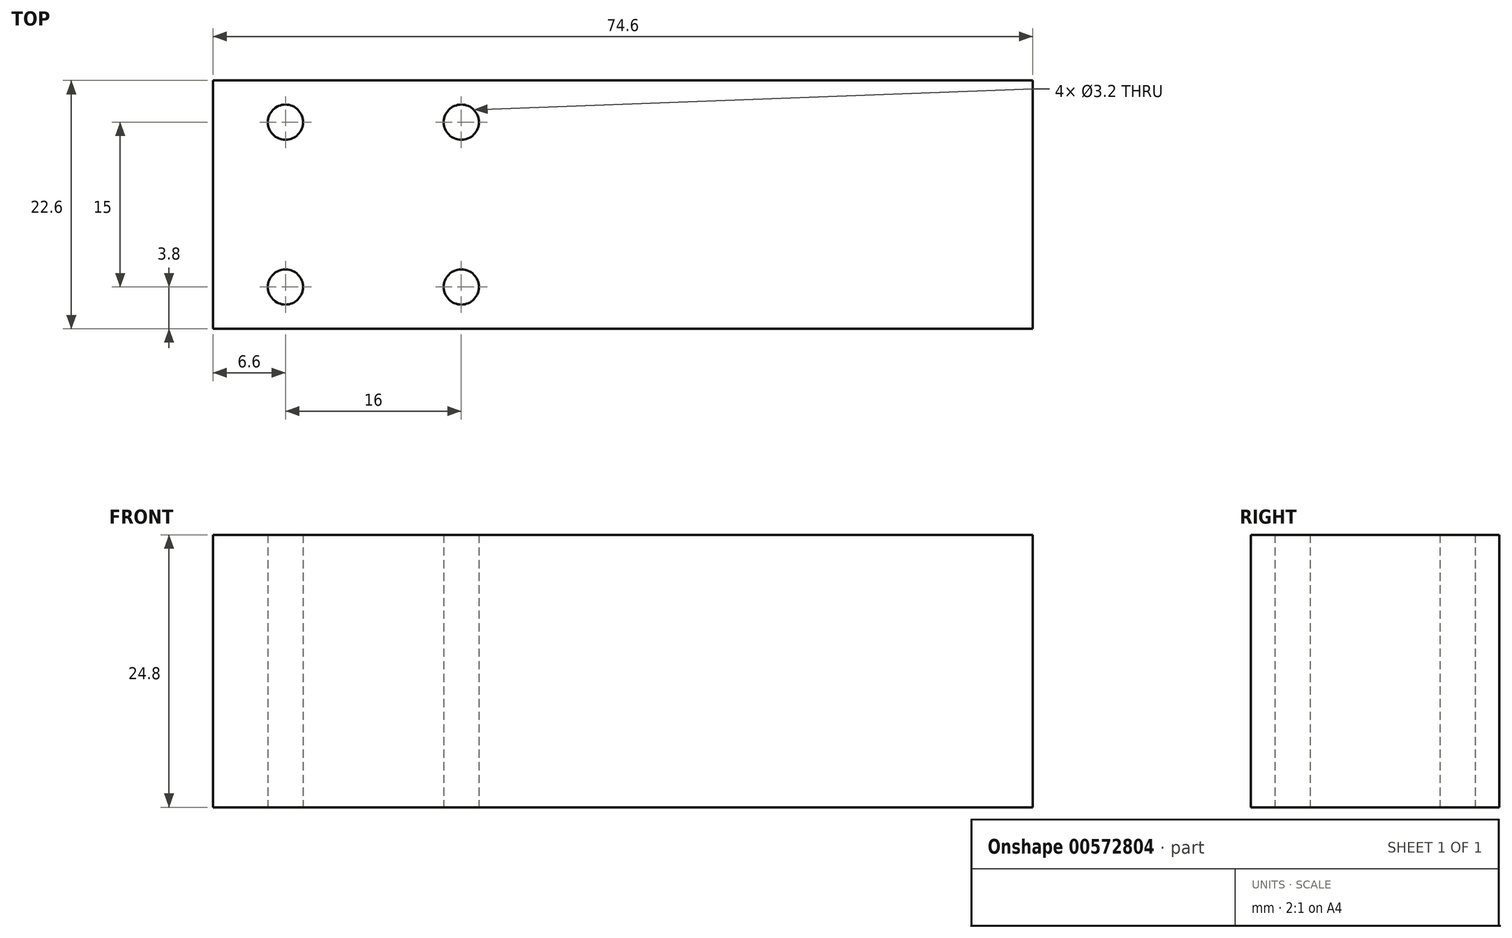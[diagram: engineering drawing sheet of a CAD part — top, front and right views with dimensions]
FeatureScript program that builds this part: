
annotation { "Feature Type Name" : "Feature", "Feature Type Description" : "" }
export const myFeature = defineFeature(function(context is Context, id is Id, definition is map)
    precondition{}
    {
        {
            var Q0;
            Q0=qCreatedBy(makeId("Top.planeOp"),FACE);
            var sketch = newSketch(context, id + "F0", { "sketchPlane" : qUnion([Q0])});
            skLineSegment(sketch, "E0.bottom", {"start": v(0, 0) * mm, "end": v(-37.6, 0) * mm});
            skLineSegment(sketch, "E0.top", {"start": v(0, -22.6) * mm, "end": v(-37.6, -22.6) * mm});
            skLineSegment(sketch, "E0.left", {"start": v(0, 0) * mm, "end": v(0, -22.6) * mm, "construction": true});
            skLineSegment(sketch, "E0.right", {"start": v(-37.6, 0) * mm, "end": v(-37.6, -22.6) * mm});
            skCircle(sketch, "E1", {"center": v(-31, -3.8) * mm, "radius": 1.6 * mm});
            skCircle(sketch, "E2", {"center": v(-15, -3.8) * mm, "radius": 1.6 * mm});
            skCircle(sketch, "E3", {"center": v(-31, -18.8) * mm, "radius": 1.6 * mm});
            skCircle(sketch, "E4", {"center": v(-15, -18.8) * mm, "radius": 1.6 * mm});
            skLineSegment(sketch, "E5", {"start": v(-49.07, -11.3) * mm, "end": v(22.15, -11.3) * mm, "construction": true});
            skLineSegment(sketch, "E6.bottom", {"start": v(0, -22.6) * mm, "end": v(37, -22.6) * mm});
            skLineSegment(sketch, "E6.top", {"start": v(0, 0) * mm, "end": v(37, 0) * mm});
            skLineSegment(sketch, "E6.right", {"start": v(37, -22.6) * mm, "end": v(37, 0) * mm});
            skSolve(sketch);
        }
        {
            var Q0;
            Q0 = qSketchRegion(id + "F0", true);
            extrude(context, id + "F1", {"entities" : qUnion([Q0]), "depth" : 24.8 * mm, "offsetDistance" : 25 * mm});
        }
    });
